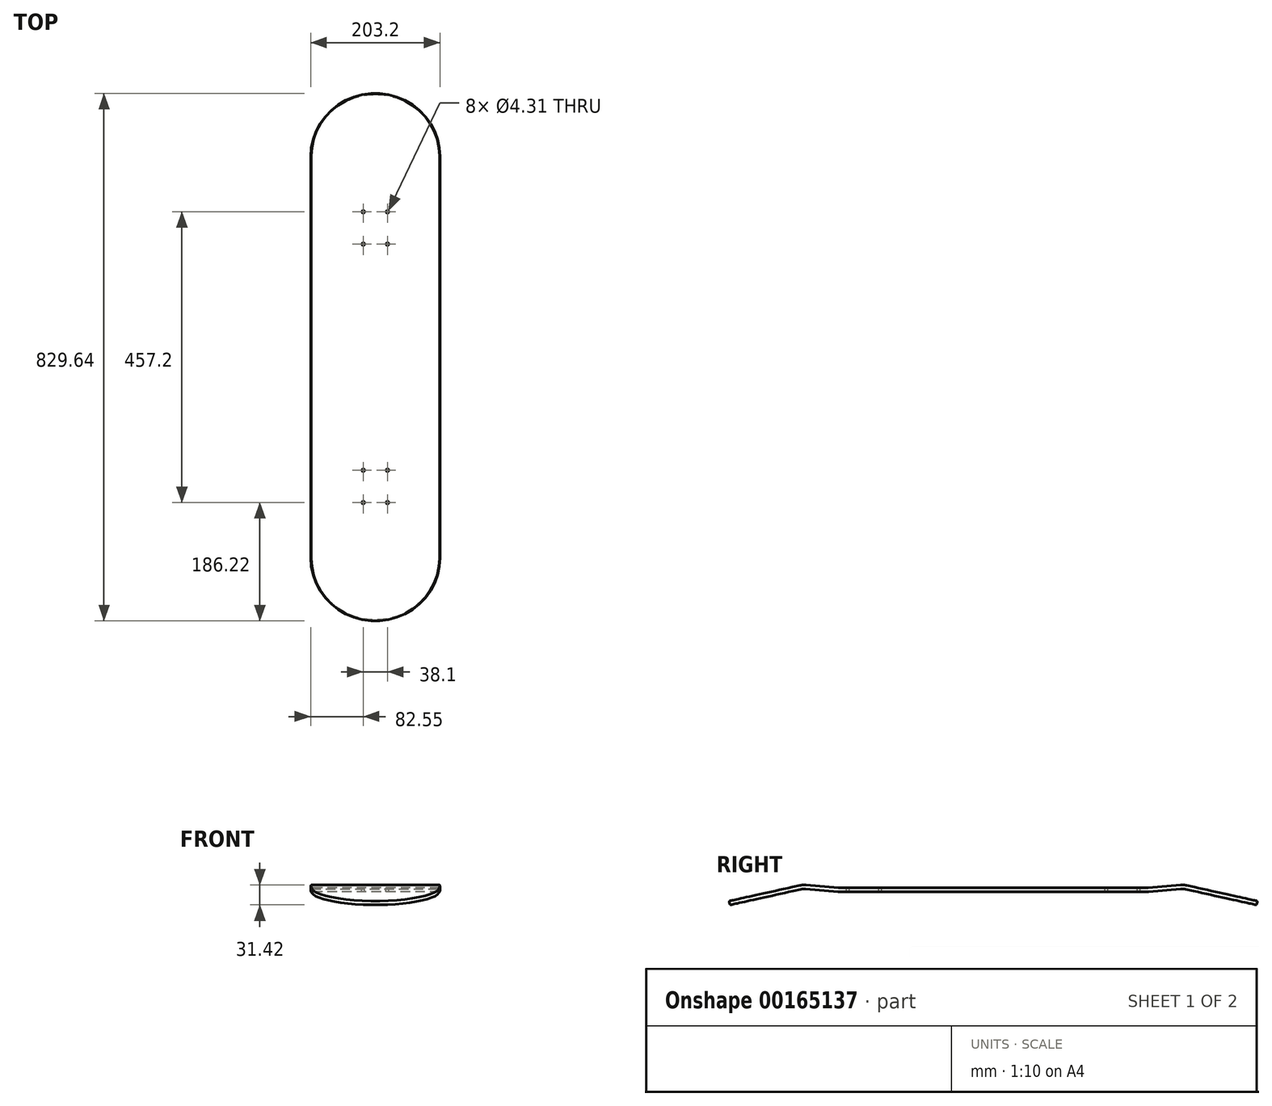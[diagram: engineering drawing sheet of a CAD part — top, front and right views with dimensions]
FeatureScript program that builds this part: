
annotation { "Feature Type Name" : "Feature", "Feature Type Description" : "" }
export const myFeature = defineFeature(function(context is Context, id is Id, definition is map)
    precondition{}
    {
        {
            var Q0;
            Q0=qCreatedBy(makeId("Top.planeOp"),FACE);
            var sketch = newSketch(context, id + "F0", { "sketchPlane" : qUnion([Q0])});
            skLineSegment(sketch, "E0.bottom", {"start": v(101.6, 241.3) * mm, "end": v(-101.6, 241.3) * mm});
            skLineSegment(sketch, "E0.top", {"start": v(101.6, -241.3) * mm, "end": v(-101.6, -241.3) * mm});
            skLineSegment(sketch, "E0.left", {"start": v(101.6, 241.3) * mm, "end": v(101.6, -241.3) * mm});
            skLineSegment(sketch, "E0.right", {"start": v(-101.6, 241.3) * mm, "end": v(-101.6, -241.3) * mm});
            skPoint(sketch, "E0.middle", {"position": v(0, 0) * mm});
            skSolve(sketch);
        }
        {
            var Q0;
            Q0=makeQuery(id+"F0.imprint","IMPRINT",FACE,{"disambiguationData":[TD([[makeQuery(id+"F0.imprint","IMPRINT",EDGE,{"derivedFrom":sQuery(id+"F0.wireOp",EDGE,"E0.bottom")}),1.0]])]});
            extrude(context, id + "F1", {"entities" : qUnion([Q0]), "depth" : 6.35 * mm});
        }
        {
            var Q0;
            Q0=makeQuery(id+"F1.opExtrude","SWEPT_FACE",FACE,{"disambiguationData":[OSD([sQuery(id+"F0.wireOp",EDGE,"E0.bottom")])]});
            var sketch = newSketch(context, id + "F2", { "sketchPlane" : qUnion([Q0])});
            skLineSegment(sketch, "E1.bottom", {"start": v(-100.8, 0) * mm, "end": v(-107.16, 0) * mm});
            skLineSegment(sketch, "E1.top", {"start": v(-100.8, 6.35) * mm, "end": v(-107.16, 6.35) * mm});
            skLineSegment(sketch, "E1.left", {"start": v(-100.8, 0) * mm, "end": v(-100.8, 6.35) * mm, "construction": true});
            skLineSegment(sketch, "E1.right", {"start": v(-107.16, 0) * mm, "end": v(-107.16, 6.35) * mm});
            skLineSegment(sketch, "E2", {"start": v(-100.8, 3.18) * mm, "end": v(-101.6, 3.18) * mm, "construction": true});
            skArc(sketch, "E3", {"start": v(-100.8, 6.35) * mm, "mid": v(-101.6, 3.17) * mm, "end": v(-100.8, 0) * mm});
            skSolve(sketch);
        }
        {
            var Q0;
            Q0=makeQuery(id+"F1.opExtrude","SWEPT_FACE",FACE,{"disambiguationData":[OSD([sQuery(id+"F0.wireOp",EDGE,"E0.left")])]});
            var sketch = newSketch(context, id + "F3", { "sketchPlane" : qUnion([Q0])});
            skLineSegment(sketch, "E4", {"start": v(241.3, 6.35) * mm, "end": v(241.3, 0) * mm});
            skArc(sketch, "E5", {"start": v(241.3, 0) * mm, "mid": v(242.68, 0.03) * mm, "end": v(244.07, 0.12) * mm});
            skArc(sketch, "E6", {"start": v(241.3, 6.35) * mm, "mid": v(242.4, 6.37) * mm, "end": v(243.51, 6.45) * mm});
            skLineSegment(sketch, "E7", {"start": v(241.3, 0) * mm, "end": v(296.89, 0) * mm, "construction": true});
            skLineSegment(sketch, "E8.bottom", {"start": v(243.51, 6.45) * mm, "end": v(294.12, 10.87) * mm});
            skLineSegment(sketch, "E8.top", {"start": v(244.07, 0.12) * mm, "end": v(294.67, 4.55) * mm});
            skLineSegment(sketch, "E8.left", {"start": v(243.51, 6.45) * mm, "end": v(244.07, 0.12) * mm, "construction": true});
            skLineSegment(sketch, "E8.right", {"start": v(294.12, 10.87) * mm, "end": v(294.67, 4.55) * mm, "construction": true});
            skLineSegment(sketch, "E9", {"start": v(241.3, 31.75) * mm, "end": v(243.51, 6.45) * mm, "construction": true});
            skArc(sketch, "E10", {"start": v(302.37, 4.05) * mm, "mid": v(298.54, 4.6) * mm, "end": v(294.67, 4.55) * mm});
            skArc(sketch, "E11", {"start": v(303.74, 10.25) * mm, "mid": v(298.95, 10.93) * mm, "end": v(294.12, 10.87) * mm});
            skLineSegment(sketch, "E12.bottom", {"start": v(302.37, 4.05) * mm, "end": v(413.98, -20.6) * mm});
            skLineSegment(sketch, "E12.top", {"start": v(303.74, 10.25) * mm, "end": v(415.35, -14.4) * mm});
            skLineSegment(sketch, "E12.left", {"start": v(302.37, 4.05) * mm, "end": v(303.74, 10.25) * mm, "construction": true});
            skLineSegment(sketch, "E12.right", {"start": v(413.98, -20.6) * mm, "end": v(415.35, -14.4) * mm});
            skLineSegment(sketch, "E13", {"start": v(296.89, 11) * mm, "end": v(415.35, 11) * mm, "construction": true});
            skLineSegment(sketch, "E14", {"start": v(415.35, 11) * mm, "end": v(415.35, -14.4) * mm, "construction": true});
            skLineSegment(sketch, "E15", {"start": v(296.89, 0) * mm, "end": v(296.89, 11) * mm, "construction": true});
            skArc(sketch, "E16", {"start": v(-244.07, 0.12) * mm, "mid": v(-242.68, 0.03) * mm, "end": v(-241.3, 0) * mm});
            skArc(sketch, "E17", {"start": v(-243.51, 6.45) * mm, "mid": v(-242.4, 6.37) * mm, "end": v(-241.3, 6.35) * mm});
            skLineSegment(sketch, "E18", {"start": v(-241.3, 0) * mm, "end": v(-241.3, 6.35) * mm});
            skLineSegment(sketch, "E19.bottom", {"start": v(-244.07, 0.12) * mm, "end": v(-294.67, 4.55) * mm});
            skLineSegment(sketch, "E19.top", {"start": v(-243.51, 6.45) * mm, "end": v(-294.12, 10.87) * mm});
            skLineSegment(sketch, "E19.left", {"start": v(-244.07, 0.12) * mm, "end": v(-243.51, 6.45) * mm, "construction": true});
            skLineSegment(sketch, "E19.right", {"start": v(-294.67, 4.55) * mm, "end": v(-294.12, 10.87) * mm, "construction": true});
            skArc(sketch, "E20", {"start": v(-294.67, 4.55) * mm, "mid": v(-298.54, 4.6) * mm, "end": v(-302.37, 4.05) * mm});
            skArc(sketch, "E21", {"start": v(-294.12, 10.87) * mm, "mid": v(-298.95, 10.93) * mm, "end": v(-303.74, 10.25) * mm});
            skLineSegment(sketch, "E22.bottom", {"start": v(-302.37, 4.05) * mm, "end": v(-413.98, -20.6) * mm});
            skLineSegment(sketch, "E22.top", {"start": v(-303.74, 10.25) * mm, "end": v(-415.35, -14.4) * mm});
            skLineSegment(sketch, "E22.left", {"start": v(-302.37, 4.05) * mm, "end": v(-303.74, 10.25) * mm, "construction": true});
            skLineSegment(sketch, "E22.right", {"start": v(-413.98, -20.6) * mm, "end": v(-415.35, -14.4) * mm});
            skLineSegment(sketch, "E23", {"start": v(294.67, 4.55) * mm, "end": v(-294.67, 4.55) * mm, "construction": true});
            skLineSegment(sketch, "E24", {"start": v(0, 6.35) * mm, "end": v(0, 4.55) * mm, "construction": true});
            skLineSegment(sketch, "E25", {"start": v(413.98, -20.6) * mm, "end": v(-413.98, -20.6) * mm, "construction": true});
            skSolve(sketch);
        }
        {
            var Q0;
            Q0=makeQuery(id+"F3.imprint","IMPRINT",FACE,{"disambiguationData":[TD([[makeQuery(id+"F3.imprint","IMPRINT",EDGE,{"derivedFrom":sQuery(id+"F3.wireOp",EDGE,"E4")}),1.0]])]});
            var Q1;
            Q1=makeQuery(id+"F3.imprint","IMPRINT",FACE,{"disambiguationData":[TD([[makeQuery(id+"F3.imprint","IMPRINT",EDGE,{"derivedFrom":sQuery(id+"F3.wireOp",EDGE,"E16")}),1.0]])]});
            var Q2;
            Q2=makeQuery(id+"F1.opExtrude","SWEPT_FACE",FACE,{"disambiguationData":[OSD([sQuery(id+"F0.wireOp",EDGE,"E0.right")])]});
            extrude(context, id + "F4", {"entities" : qUnion([Q0, Q1]), "operationType" : NewBodyOperationType.ADD, "endBound" : BoundingType.UP_TO_SURFACE, "oppositeDirection" : true, "endBoundEntityFace" : qUnion([Q2]), "depth" : 25.4 * mm});
        }
        {
            var Q0;
            Q0=makeQuery(id+"F4.opExtrude","CAP_EDGE",EDGE,{"disambiguationData":[OSD([sQuery(id+"F3.wireOp",EDGE,"E12.right")])],"isStart":true});
            var Q1;
            Q1=makeQuery(id+"F4.opExtrude","CAP_EDGE",EDGE,{"disambiguationData":[OSD([sQuery(id+"F3.wireOp",EDGE,"E12.right")])],"isStart":false});
            var Q2;
            Q2=makeQuery(id+"F4.opExtrude","CAP_EDGE",EDGE,{"disambiguationData":[OSD([sQuery(id+"F3.wireOp",EDGE,"E22.right")])],"isStart":true});
            var Q3;
            Q3=makeQuery(id+"F4.opExtrude","CAP_EDGE",EDGE,{"disambiguationData":[OSD([sQuery(id+"F3.wireOp",EDGE,"E22.right")])],"isStart":false});
            fillet(context, id + "F5", {"entities" : qUnion([Q0, Q1, Q2, Q3]), "radius" : 101.6 * mm, "tangentPropagation" : true, "allowEdgeOverflow" : false});
        }
        {
            var Q0;
            Q0=qSketchRegion(id+"F2",true);
            var Q1;
            Q1=makeQuery(id+"F1.opExtrude","CAP_EDGE",EDGE,{"disambiguationData":[OSD([sQuery(id+"F0.wireOp",EDGE,"E0.left")])],"isStart":true});
            var Q2;
            Q2=makeQuery(id+"F4.opExtrude","CAP_EDGE",EDGE,{"disambiguationData":[OSD([sQuery(id+"F3.wireOp",EDGE,"E16")])],"isStart":true});
            var Q3;
            Q3=makeQuery(id+"F4.opExtrude","CAP_EDGE",EDGE,{"disambiguationData":[OSD([sQuery(id+"F3.wireOp",EDGE,"E19.bottom")])],"isStart":true});
            var Q4;
            Q4=makeQuery(id+"F4.opExtrude","CAP_EDGE",EDGE,{"disambiguationData":[OSD([sQuery(id+"F3.wireOp",EDGE,"E20")])],"isStart":true});
            var Q5;
            Q5=makeQuery(id+"F4.opExtrude","CAP_EDGE",EDGE,{"disambiguationData":[OSD([sQuery(id+"F3.wireOp",EDGE,"E22.bottom")])],"isStart":true});
            var Q6;
            Q6=makeQuery(id+"F5.opFillet","BLEND_EDGE",EDGE,{"blendedFrom":[makeQuery(id+"F4.opExtrude","CAP_EDGE",EDGE,{"disambiguationData":[OSD([sQuery(id+"F3.wireOp",EDGE,"E22.right")])],"isStart":true}),makeQuery(id+"F4.opExtrude","SWEPT_FACE",FACE,{"disambiguationData":[OSD([sQuery(id+"F3.wireOp",EDGE,"E22.bottom")])]})],"blendedInto":[makeQuery(id+"F4.opExtrude","SWEPT_FACE",FACE,{"disambiguationData":[OSD([sQuery(id+"F3.wireOp",EDGE,"E22.bottom")])]})]});
            var Q7;
            Q7=makeQuery(id+"F4.opExtrude","CAP_EDGE",EDGE,{"disambiguationData":[OSD([sQuery(id+"F3.wireOp",EDGE,"E22.bottom")])],"isStart":false});
            var Q8;
            Q8=makeQuery(id+"F4.opExtrude","CAP_EDGE",EDGE,{"disambiguationData":[OSD([sQuery(id+"F3.wireOp",EDGE,"E20")])],"isStart":false});
            var Q9;
            Q9=makeQuery(id+"F4.opExtrude","CAP_EDGE",EDGE,{"disambiguationData":[OSD([sQuery(id+"F3.wireOp",EDGE,"E19.bottom")])],"isStart":false});
            var Q10;
            Q10=makeQuery(id+"F4.opExtrude","CAP_EDGE",EDGE,{"disambiguationData":[OSD([sQuery(id+"F3.wireOp",EDGE,"E16")])],"isStart":false});
            var Q11;
            Q11=makeQuery(id+"F1.opExtrude","CAP_EDGE",EDGE,{"disambiguationData":[OSD([sQuery(id+"F0.wireOp",EDGE,"E0.right")])],"isStart":true});
            var Q12;
            Q12=makeQuery(id+"F4.opExtrude","CAP_EDGE",EDGE,{"disambiguationData":[OSD([sQuery(id+"F3.wireOp",EDGE,"E5")])],"isStart":false});
            var Q13;
            Q13=makeQuery(id+"F4.opExtrude","CAP_EDGE",EDGE,{"disambiguationData":[OSD([sQuery(id+"F3.wireOp",EDGE,"E8.top")])],"isStart":false});
            var Q14;
            Q14=makeQuery(id+"F4.opExtrude","CAP_EDGE",EDGE,{"disambiguationData":[OSD([sQuery(id+"F3.wireOp",EDGE,"E10")])],"isStart":false});
            var Q15;
            Q15=makeQuery(id+"F4.opExtrude","CAP_EDGE",EDGE,{"disambiguationData":[OSD([sQuery(id+"F3.wireOp",EDGE,"E12.bottom")])],"isStart":false});
            var Q16;
            Q16=makeQuery(id+"F5.opFillet","BLEND_EDGE",EDGE,{"blendedFrom":[makeQuery(id+"F4.opExtrude","CAP_EDGE",EDGE,{"disambiguationData":[OSD([sQuery(id+"F3.wireOp",EDGE,"E12.right")])],"isStart":true}),makeQuery(id+"F4.opExtrude","SWEPT_FACE",FACE,{"disambiguationData":[OSD([sQuery(id+"F3.wireOp",EDGE,"E12.bottom")])]})],"blendedInto":[makeQuery(id+"F4.opExtrude","SWEPT_FACE",FACE,{"disambiguationData":[OSD([sQuery(id+"F3.wireOp",EDGE,"E12.bottom")])]})]});
            var Q17;
            Q17=makeQuery(id+"F4.opExtrude","CAP_EDGE",EDGE,{"disambiguationData":[OSD([sQuery(id+"F3.wireOp",EDGE,"E12.bottom")])],"isStart":true});
            var Q18;
            Q18=makeQuery(id+"F4.opExtrude","CAP_EDGE",EDGE,{"disambiguationData":[OSD([sQuery(id+"F3.wireOp",EDGE,"E10")])],"isStart":true});
            var Q19;
            Q19=makeQuery(id+"F4.opExtrude","CAP_EDGE",EDGE,{"disambiguationData":[OSD([sQuery(id+"F3.wireOp",EDGE,"E8.top")])],"isStart":true});
            var Q20;
            Q20=makeQuery(id+"F4.opExtrude","CAP_EDGE",EDGE,{"disambiguationData":[OSD([sQuery(id+"F3.wireOp",EDGE,"E5")])],"isStart":true});
            sweep(context, id + "F6", {"operationType" : NewBodyOperationType.REMOVE, "profiles" : qUnion([Q0]), "path" : qUnion([Q1, Q2, Q3, Q4, Q5, Q6, Q7, Q8, Q9, Q10, Q11, Q12, Q13, Q14, Q15, Q16, Q17, Q18, Q19, Q20])});
        }
        {
            var Q0;
            Q0=makeQuery(id+"F1.opExtrude","CAP_FACE",FACE,{"disambiguationData":[OSD([sQuery(id+"F0.wireOp",EDGE,"E0.bottom"),sQuery(id+"F0.wireOp",EDGE,"E0.top"),sQuery(id+"F0.wireOp",EDGE,"E0.left"),sQuery(id+"F0.wireOp",EDGE,"E0.right")])],"isStart":false});
            var sketch = newSketch(context, id + "F7", { "sketchPlane" : qUnion([Q0])});
            skLineSegment(sketch, "E26", {"start": v(0, 241.3) * mm, "end": v(0, 228.6) * mm, "construction": true});
            skLineSegment(sketch, "E27", {"start": v(0, -241.3) * mm, "end": v(0, -228.6) * mm, "construction": true});
            skLineSegment(sketch, "E28.bottom", {"start": v(-19.05, 228.6) * mm, "end": v(19.05, 228.6) * mm, "construction": true});
            skLineSegment(sketch, "E28.top", {"start": v(-19.05, 177.8) * mm, "end": v(19.05, 177.8) * mm, "construction": true});
            skLineSegment(sketch, "E28.left", {"start": v(-19.05, 228.6) * mm, "end": v(-19.05, 177.8) * mm, "construction": true});
            skLineSegment(sketch, "E28.right", {"start": v(19.05, 228.6) * mm, "end": v(19.05, 177.8) * mm, "construction": true});
            skLineSegment(sketch, "E29.bottom", {"start": v(-19.05, -228.6) * mm, "end": v(19.05, -228.6) * mm, "construction": true});
            skLineSegment(sketch, "E29.top", {"start": v(-19.05, -177.8) * mm, "end": v(19.05, -177.8) * mm, "construction": true});
            skLineSegment(sketch, "E29.left", {"start": v(-19.05, -228.6) * mm, "end": v(-19.05, -177.8) * mm, "construction": true});
            skLineSegment(sketch, "E29.right", {"start": v(19.05, -228.6) * mm, "end": v(19.05, -177.8) * mm, "construction": true});
            skCircle(sketch, "E30", {"center": v(-19.05, 228.6) * mm, "radius": 2.15 * mm});
            skCircle(sketch, "E31", {"center": v(19.05, 228.6) * mm, "radius": 2.15 * mm});
            skCircle(sketch, "E32", {"center": v(19.05, 177.8) * mm, "radius": 2.15 * mm});
            skCircle(sketch, "E33", {"center": v(-19.05, 177.8) * mm, "radius": 2.15 * mm});
            skCircle(sketch, "E34", {"center": v(19.05, -177.8) * mm, "radius": 2.15 * mm});
            skCircle(sketch, "E35", {"center": v(-19.05, -177.8) * mm, "radius": 2.15 * mm});
            skCircle(sketch, "E36", {"center": v(-19.05, -228.6) * mm, "radius": 2.15 * mm});
            skCircle(sketch, "E37", {"center": v(19.05, -228.6) * mm, "radius": 2.15 * mm});
            skSolve(sketch);
        }
        {
            var Q0;
            Q0=qSketchRegion(id+"F7",true);
            var Q1;
            Q1=makeQuery(id+"F1.opExtrude","CAP_FACE",FACE,{"disambiguationData":[OSD([sQuery(id+"F0.wireOp",EDGE,"E0.bottom"),sQuery(id+"F0.wireOp",EDGE,"E0.top"),sQuery(id+"F0.wireOp",EDGE,"E0.left"),sQuery(id+"F0.wireOp",EDGE,"E0.right")])],"isStart":true});
            extrude(context, id + "F8", {"entities" : qUnion([Q0]), "operationType" : NewBodyOperationType.REMOVE, "endBound" : BoundingType.UP_TO_SURFACE, "oppositeDirection" : true, "endBoundEntityFace" : qUnion([Q1]), "depth" : 25.4 * mm});
        }
    });
